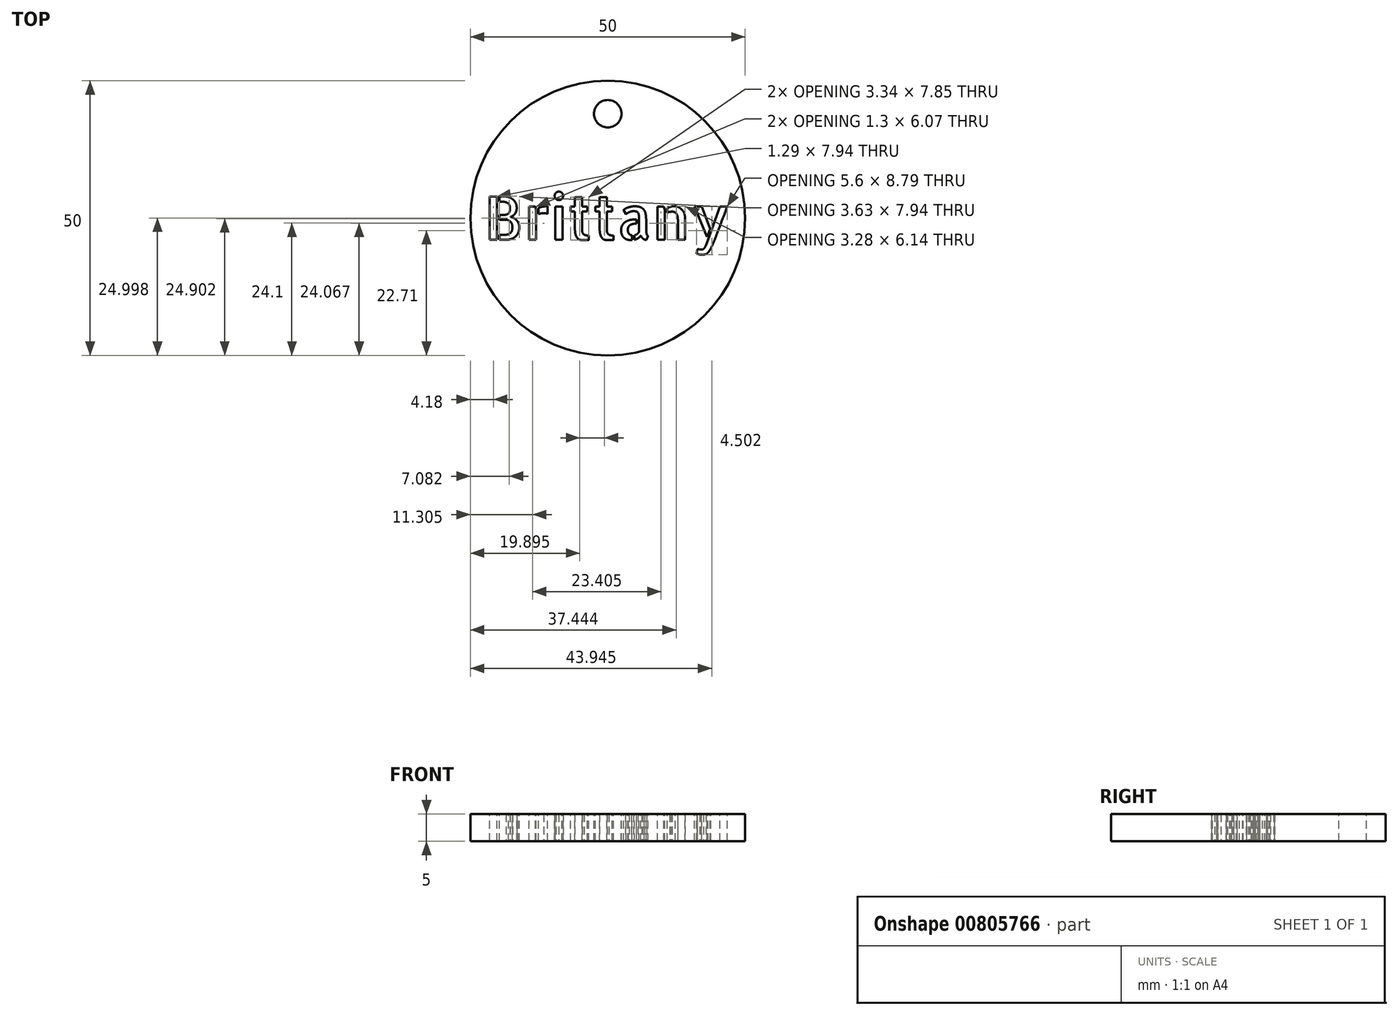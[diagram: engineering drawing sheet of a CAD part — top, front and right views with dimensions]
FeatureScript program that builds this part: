
annotation { "Feature Type Name" : "Feature", "Feature Type Description" : "" }
export const myFeature = defineFeature(function(context is Context, id is Id, definition is map)
    precondition{}
    {
        {
            var Q0;
            Q0=qCreatedBy(makeId("Top.planeOp"),FACE);
            var sketch = newSketch(context, id + "F0", { "sketchPlane" : qUnion([Q0])});
            skCircle(sketch, "E0", {"center": v(0, 0) * mm, "radius": 25 * mm});
            skCircle(sketch, "E1", {"center": v(0, 19) * mm, "radius": 2.5 * mm});
            skLineSegment(sketch, "E2", {"start": v(0, 0) * mm, "end": v(0, 19) * mm, "construction": true});
            skSolve(sketch);
        }
        {
            var Q0;
            Q0=makeQuery(id+"F0.imprint","IMPRINT",FACE,{"disambiguationData":[TD([[makeQuery(id+"F0.imprint","IMPRINT",EDGE,{"derivedFrom":sQuery(id+"F0.wireOp",EDGE,"E0")}),1.0]])]});
            extrude(context, id + "F1", {"entities" : qUnion([Q0]), "oppositeDirection" : true, "depth" : 5 * mm, "offsetDistance" : 25 * mm});
        }
        {
            var Q0;
            Q0=makeQuery(id+"F1.opExtrude","CAP_FACE",FACE,{"disambiguationData":[OSD([sQuery(id+"F0.wireOp",EDGE,"E0"),sQuery(id+"F0.wireOp",EDGE,"E1")])],"isStart":true});
            var sketch = newSketch(context, id + "F2", { "sketchPlane" : qUnion([Q0])});
            skText(sketch, "E3", { "text": "Brittany", "fontName": "AllertaStencil-Regular.ttf"});
            skLineSegment(sketch, "E4", {"start": v(0, 0) * mm, "end": v(0, 3.97) * mm, "construction": true});
            skLineSegment(sketch, "E5", {"start": v(0, 0) * mm, "end": v(22.5, 0) * mm, "construction": true});
            const initialGuessF2  = {"E3": [-0.0225, -0.00397, 1, 0, 0.00794]};
            skSetInitialGuess(sketch, initialGuessF2);
            skSolve(sketch);
        }
        {
            var Q0;
            Q0 = qSketchRegion(id + "F2", true);
            extrude(context, id + "F3", {"entities" : qUnion([Q0]), "operationType" : NewBodyOperationType.REMOVE, "oppositeDirection" : true, "depth" : 25 * mm, "offsetDistance" : 25 * mm});
        }
    });
